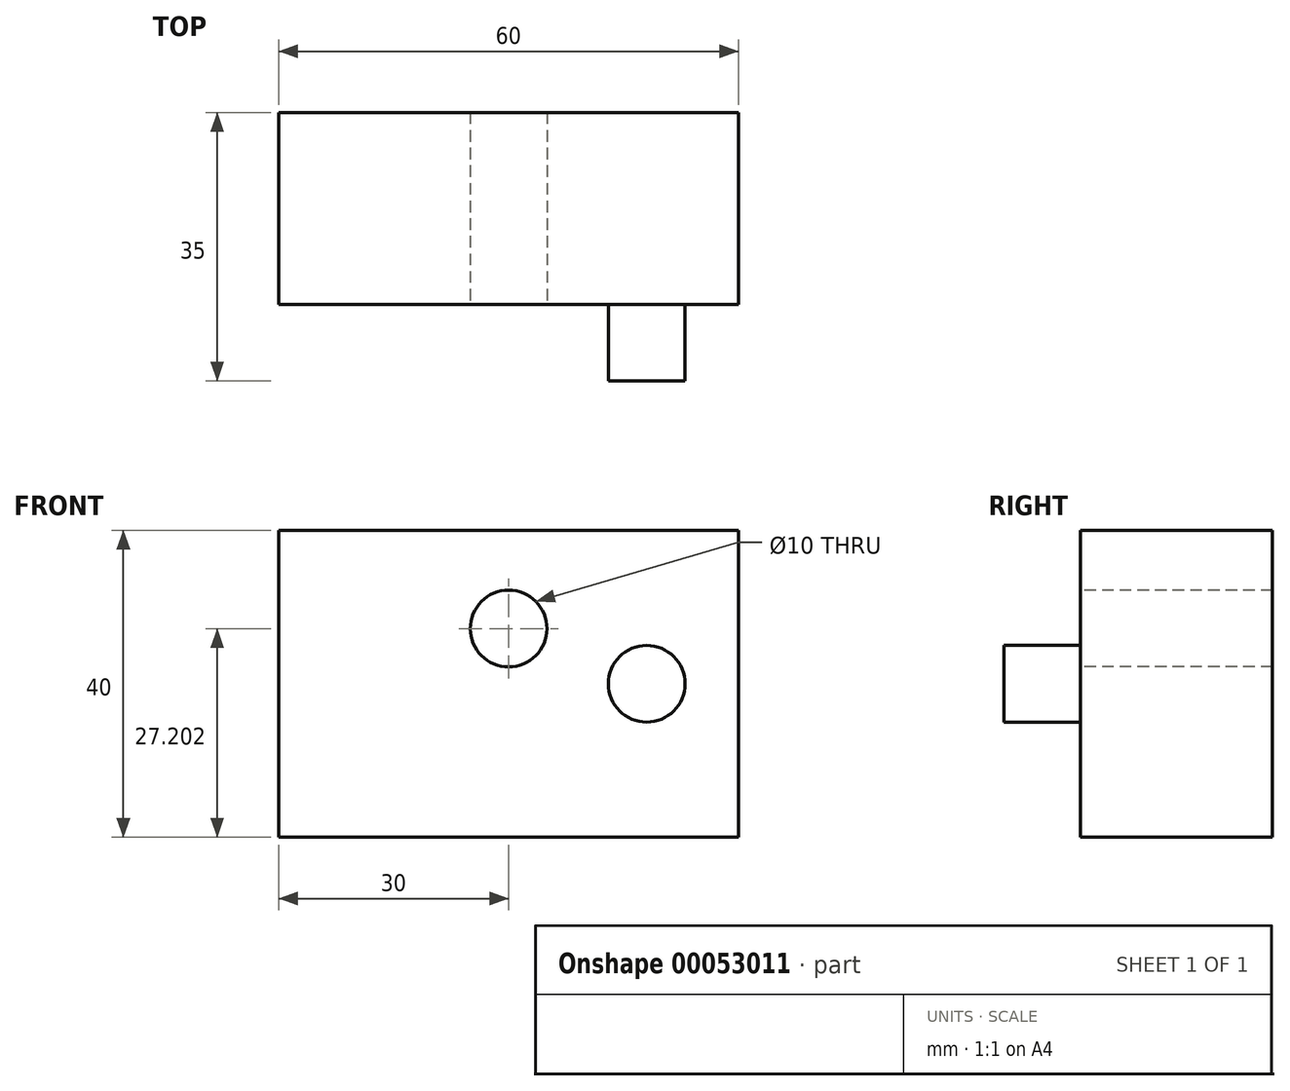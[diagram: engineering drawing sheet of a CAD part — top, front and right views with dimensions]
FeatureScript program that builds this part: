
annotation { "Feature Type Name" : "Feature", "Feature Type Description" : "" }
export const myFeature = defineFeature(function(context is Context, id is Id, definition is map)
    precondition{}
    {
        {
            var Q0;
            Q0=qCreatedBy(makeId("Front.planeOp"),FACE);
            var sketch = newSketch(context, id + "F0", { "sketchPlane" : qUnion([Q0])});
            skLineSegment(sketch, "E0.rect.bottom", {"start": v(30, 20) * mm, "end": v(-30, 20) * mm});
            skLineSegment(sketch, "E0.rect.top", {"start": v(30, -20) * mm, "end": v(-30, -20) * mm});
            skLineSegment(sketch, "E0.rect.left", {"start": v(30, 20) * mm, "end": v(30, -20) * mm});
            skLineSegment(sketch, "E0.rect.right", {"start": v(-30, 20) * mm, "end": v(-30, -20) * mm});
            skPoint(sketch, "E0.rect.middle", {"position": v(0, 0) * mm});
            skSolve(sketch);
        }
        {
            var Q0;
            Q0=makeQuery(id+"F0.imprint","IMPRINT",FACE,{"disambiguationData":[TD([[makeQuery(id+"F0.imprint","IMPRINT",EDGE,{"derivedFrom":sQuery(id+"F0.wireOp",EDGE,"E0.rect.bottom")}),1.0]])]});
            extrude(context, id + "F1", {"entities" : qUnion([Q0]), "endBound" : BoundingType.SYMMETRIC, "depth" : 25 * mm});
        }
        {
            var Q0;
            Q0=makeQuery(id+"F1.opExtrude","CAP_FACE",FACE,{"disambiguationData":[OSD([sQuery(id+"F0.wireOp",EDGE,"E0.rect.bottom"),sQuery(id+"F0.wireOp",EDGE,"E0.rect.top"),sQuery(id+"F0.wireOp",EDGE,"E0.rect.left"),sQuery(id+"F0.wireOp",EDGE,"E0.rect.right")])],"isStart":false});
            var sketch = newSketch(context, id + "F2", { "sketchPlane" : qUnion([Q0])});
            skCircle(sketch, "E1", {"center": v(18, 0) * mm, "radius": 5 * mm});
            skSolve(sketch);
        }
        {
            var Q0;
            Q0=makeQuery(id+"F2.imprint","IMPRINT",FACE,{"disambiguationData":[TD([[makeQuery(id+"F2.imprint","IMPRINT",EDGE,{"derivedFrom":sQuery(id+"F2.wireOp",EDGE,"c30986a0-4118-49dc-861e-8dfdec2b827a")}),1.0]])]});
            var Q1;
            Q1=makeQuery(id+"F2.imprint","IMPRINT",FACE,{"disambiguationData":[TD([[makeQuery(id+"F2.imprint","IMPRINT",EDGE,{"derivedFrom":sQuery(id+"F2.wireOp",EDGE,"E1")}),1.0]])]});
            extrude(context, id + "F3", {"entities" : qUnion([Q0, Q1]), "operationType" : NewBodyOperationType.ADD, "depth" : 10 * mm});
        }
        {
            var Q0;
            Q0=makeQuery(id+"F1.opExtrude","CAP_FACE",FACE,{"disambiguationData":[OSD([sQuery(id+"F0.wireOp",EDGE,"E0.rect.bottom"),sQuery(id+"F0.wireOp",EDGE,"E0.rect.top"),sQuery(id+"F0.wireOp",EDGE,"E0.rect.left"),sQuery(id+"F0.wireOp",EDGE,"E0.rect.right")])],"isStart":false});
            var sketch = newSketch(context, id + "F4", { "sketchPlane" : qUnion([Q0])});
            skCircle(sketch, "E2", {"center": v(0, 7.2) * mm, "radius": 5 * mm});
            skPoint(sketch, "E2.centerSnap0", {"position": v(0, 20) * mm});
            skSolve(sketch);
        }
        {
            var Q0;
            Q0=qSketchRegion(id+"F4",true);
            extrude(context, id + "F5", {"entities" : qUnion([Q0]), "operationType" : NewBodyOperationType.REMOVE, "oppositeDirection" : true, "depth" : 25 * mm});
        }
    });
